# Revit family: JOMA_470
name_source: partatom
category: Structural Connections
revit_build: Autodesk Revit Structure 2012 (Build: 20110309_2315(x64)
units: mm (PartAtom-declared; Revit-internal decimal feet)

## types (4) — shared parameters
Länk Joma Dimensioneringsverktyg = http://www.joma.se
Material = Varmförzinkad stålplåt
b = 55 mm  [stored 0.180446 ft]
h = 70 mm  [stored 0.229659 ft]
l = 70 mm  [stored 0.229659 ft]
zero-valued in all types: Default Elevation

## per-type parameters (varying)
| type | Med förstärkning | Typ | Utan förstärkning | Vikt | t |
| 470U000 | No | VINKEL 470U000 | Yes | 0,13 | 2.5 mm  [stored 0.0082021 ft] |
| 470M000 | Yes | VINKEL 470M000 | No | 0,132 | 2.5 mm  [stored 0.0082021 ft] |
| 470M002 | Yes | VINKEL 470M002 | No | 0,132 | 2 mm  [stored 0.00656168 ft] |
| 470U002 | No | VINKEL 470U002 | Yes | 0,13 | 2 mm  [stored 0.00656168 ft] |

note: [stored X ft] marks values corroborated as IEEE doubles in the binary element streams (Revit-internal decimal feet)

## geometry (parser evidence)
native form markers: Sweep x3
no freeform markers — native parametric forms only
